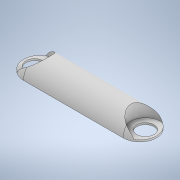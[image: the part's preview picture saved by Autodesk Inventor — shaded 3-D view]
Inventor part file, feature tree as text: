
AUTODESK INVENTOR PART (.ipt)
format: ipt  version: 2020 (Build 240168000, 168)  size: 140,800 bytes
history: native  units: in
note: dims shown in document units (in); Inventor stores cm internally (conversion verified against a paired STEP export)
features: fillet x2, sketch x2, extrude x1, hole x1
ambient origin geometry x8: Origin, YZ Plane, XZ Plane, XY Plane, X Axis, Y Axis, Z Axis, Center Point
bodies: Solid1 (feature_tree)
feature tree (6):
  extrude  "Extrusion1"  Depth=0.25in
  hole  "Hole1"  [1 undecoded]
  fillet  "Fillet1"  Radius=0.083in
  fillet  "Fillet2"  Radius=0.125in
  sketch  "Sketch1"  dims[d0=1.0in d1=0.25in]
  sketch  "Sketch2"  dims[d2=0.125in d3=0.0in d4=0.083in d5=0.083in d6=0.129in d7=0.75in d8=0.219in d9=0.112in d10=0.5635in d11=0.224in d12=0.0in d13=0.125in d14=0.125in]
note: 1 required parameter value undecoded (feature->parameter linkage not recoverable at this tier; creation-order binding heuristic only, values carry confidence <= 0.55)
